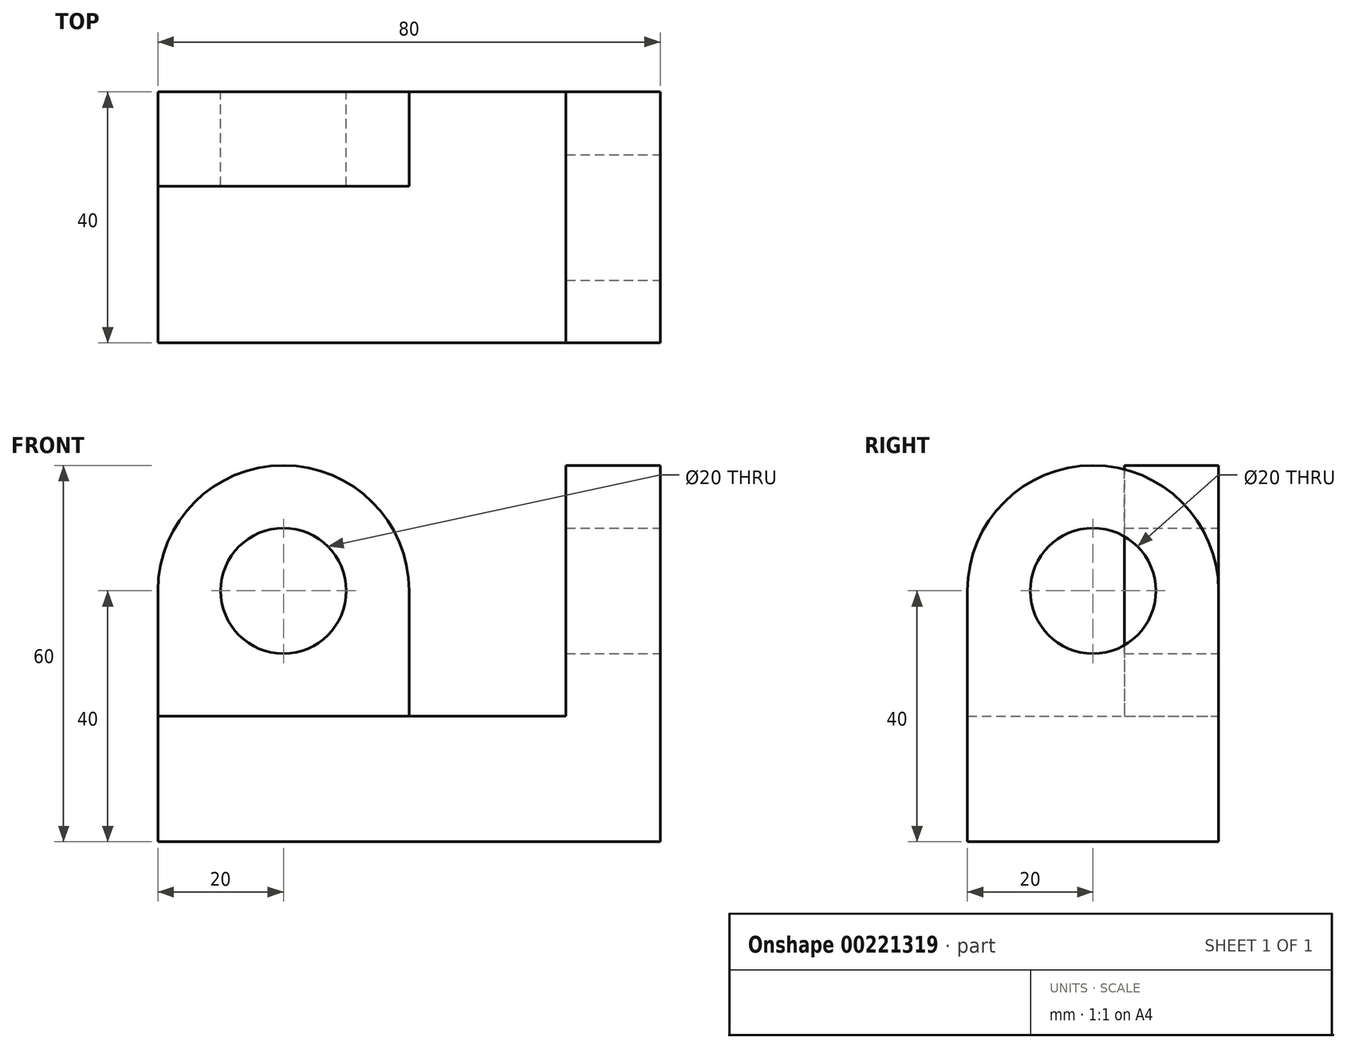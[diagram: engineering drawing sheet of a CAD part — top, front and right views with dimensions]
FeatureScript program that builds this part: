
annotation { "Feature Type Name" : "Feature", "Feature Type Description" : "" }
export const myFeature = defineFeature(function(context is Context, id is Id, definition is map)
    precondition{}
    {
        {
            var Q0;
            Q0=qCreatedBy(makeId("Front.planeOp"),FACE);
            var sketch = newSketch(context, id + "F0", { "sketchPlane" : qUnion([Q0])});
            skLineSegment(sketch, "E0", {"start": v(0, 0) * mm, "end": v(80, 0) * mm});
            skLineSegment(sketch, "E1", {"start": v(80, 0) * mm, "end": v(80, 60) * mm});
            skLineSegment(sketch, "E2", {"start": v(80, 60) * mm, "end": v(65, 60) * mm});
            skLineSegment(sketch, "E3", {"start": v(65, 60) * mm, "end": v(65, 20) * mm});
            skLineSegment(sketch, "E4", {"start": v(65, 20) * mm, "end": v(0, 20) * mm});
            skLineSegment(sketch, "E5", {"start": v(0, 20) * mm, "end": v(0, 0) * mm});
            skCircle(sketch, "E6", {"center": v(20, 40) * mm, "radius": 10 * mm});
            skArc(sketch, "E7", {"start": v(40, 40) * mm, "mid": v(20, 60) * mm, "end": v(0, 40) * mm});
            skLineSegment(sketch, "E8", {"start": v(40, 40) * mm, "end": v(40, 20) * mm});
            skLineSegment(sketch, "E9", {"start": v(0, 40) * mm, "end": v(0, 20) * mm});
            skSolve(sketch);
        }
        {
            var Q0;
            Q0=makeQuery(id+"F0.imprint","IMPRINT",FACE,{"disambiguationData":[TD([[makeQuery(id+"F0.imprint","IMPRINT",EDGE,{"derivedFrom":sQuery(id+"F0.wireOp",EDGE,"E0")}),1.0]])]});
            extrude(context, id + "F1", {"entities" : qUnion([Q0]), "depth" : 40 * mm});
        }
        {
            var Q0;
            Q0=makeQuery(id+"F0.imprint","IMPRINT",FACE,{"disambiguationData":[TD([[makeQuery(id+"F0.imprint","IMPRINT",EDGE,{"derivedFrom":sQuery(id+"F0.wireOp",EDGE,"E6")}),-1.0]])]});
            extrude(context, id + "F2", {"entities" : qUnion([Q0]), "operationType" : NewBodyOperationType.ADD, "depth" : 15 * mm});
        }
        {
            var Q0;
            Q0=makeQuery(id+"F1.opExtrude","SWEPT_FACE",FACE,{"disambiguationData":[OSD([sQuery(id+"F0.wireOp",EDGE,"E1")])]});
            var sketch = newSketch(context, id + "F3", { "sketchPlane" : qUnion([Q0])});
            skSolve(sketch);
        }
        {
            var Q0;
            Q0=makeQuery(id+"F1.opExtrude","CAP_EDGE",EDGE,{"disambiguationData":[OSD([sQuery(id+"F0.wireOp",EDGE,"E2")])],"isStart":false});
            var Q1;
            Q1=makeQuery(id+"F1.opExtrude","CAP_EDGE",EDGE,{"disambiguationData":[OSD([sQuery(id+"F0.wireOp",EDGE,"E2")])],"isStart":true});
            fillet(context, id + "F4", {"entities" : qUnion([Q0, Q1]), "radius" : 20 * mm, "tangentPropagation" : true, "allowEdgeOverflow" : false});
        }
        {
            var Q0;
            {var subQ0=sQuery(id+"F0.wireOp",EDGE,"E1");Q0=makeQuery(id+"F3.imprint","IMPRINT",FACE,{"disambiguationData":[TD([[makeQuery(id+"F3.imprint","IMPRINT",EDGE,{"derivedFrom":makeQuery(id+"F1.opExtrude","CAP_EDGE",EDGE,{"disambiguationData":[OSD([subQ0])],"isStart":true})}),1.0]])]});}
            var sketch = newSketch(context, id + "F5", { "sketchPlane" : qUnion([Q0])});
            skArc(sketch, "E10.0", {"start": v(0, 40) * mm, "mid": v(-20, 60) * mm, "end": v(-40, 40) * mm});
            skCircle(sketch, "E11", {"center": v(-20, 40) * mm, "radius": 10 * mm});
            skSolve(sketch);
        }
        {
            var Q0;
            Q0 = qSketchRegion(id + "F5", true);
            var Q1;
            Q1=makeQuery(id+"F1.opExtrude","SWEPT_FACE",FACE,{"disambiguationData":[OSD([sQuery(id+"F0.wireOp",EDGE,"E3")])]});
            extrude(context, id + "F6", {"entities" : qUnion([Q0]), "operationType" : NewBodyOperationType.REMOVE, "endBound" : BoundingType.UP_TO_SURFACE, "oppositeDirection" : true, "endBoundEntityFace" : qUnion([Q1]), "depth" : 25 * mm});
        }
    });
